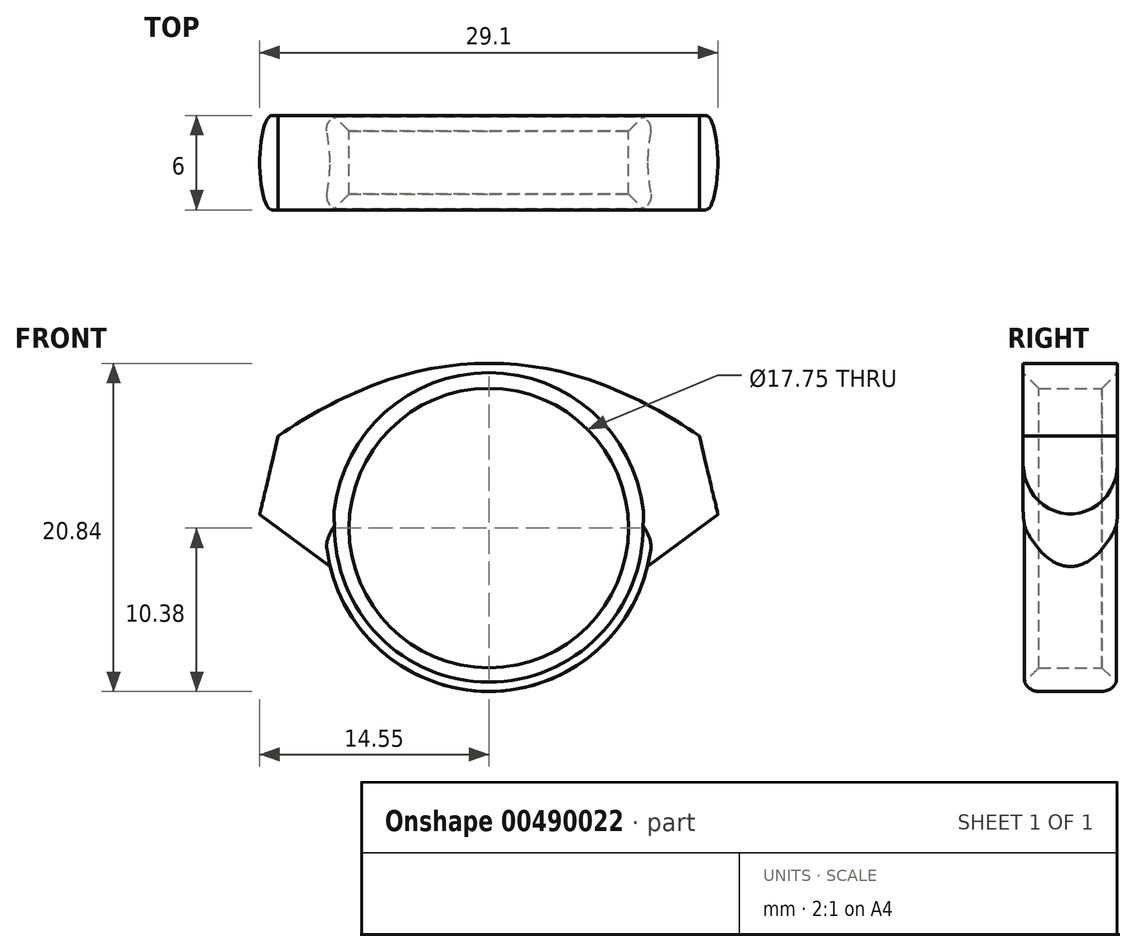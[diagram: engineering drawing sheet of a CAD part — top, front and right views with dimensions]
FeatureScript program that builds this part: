
annotation { "Feature Type Name" : "Feature", "Feature Type Description" : "" }
export const myFeature = defineFeature(function(context is Context, id is Id, definition is map)
    precondition{}
    {
        {
            var Q0;
            Q0=qCreatedBy(makeId("Front.planeOp"),FACE);
            var sketch = newSketch(context, id + "F0", { "sketchPlane" : qUnion([Q0])});
            skCircle(sketch, "E0", {"center": v(0, 0) * mm, "radius": 8.88 * mm});
            skCircle(sketch, "E1.0", {"center": v(0, 0) * mm, "radius": 10.38 * mm});
            skLineSegment(sketch, "E2", {"start": v(-10.08, -2.44) * mm, "end": v(-14.55, 0.87) * mm});
            skLineSegment(sketch, "E3", {"start": v(-14.55, 0.87) * mm, "end": v(-13.37, 5.85) * mm});
            skLineSegment(sketch, "E4", {"start": v(-13.37, 5.85) * mm, "end": v(-10.08, -2.44) * mm});
            skArc(sketch, "E5", {"start": v(0, 10.9) * mm, "mid": v(-7, 9.2) * mm, "end": v(-13.37, 5.85) * mm});
            skArc(sketch, "E6.MirrorCS", {"start": v(0, 10.9) * mm, "mid": v(7, 9.2) * mm, "end": v(13.37, 5.85) * mm});
            skLineSegment(sketch, "E7.MirrorCS", {"start": v(14.55, 0.87) * mm, "end": v(13.37, 5.85) * mm});
            skLineSegment(sketch, "E8.MirrorCS", {"start": v(10.08, -2.44) * mm, "end": v(14.55, 0.87) * mm});
            skSolve(sketch);
        }
        {
            var Q0;
            {var subQ0=sQuery(id+"F0.wireOp",EDGE,"E4");Q0=makeQuery(id+"F0.imprint","IMPRINT",FACE,{"disambiguationData":[TD([[makeQuery(id+"F0.imprint","IMPRINT",EDGE,{"derivedFrom":subQ0}),1.0]])]});}
            var Q1;
            Q1=makeQuery(id+"F0.imprint","IMPRINT",FACE,{"disambiguationData":[TD([[makeQuery(id+"F0.imprint","IMPRINT",EDGE,{"derivedFrom":sQuery(id+"F0.wireOp",EDGE,"E2")}),-1.0]])]});
            var Q2;
            Q2=makeQuery(id+"F0.imprint","IMPRINT",FACE,{"disambiguationData":[TD([[makeQuery(id+"F0.imprint","IMPRINT",EDGE,{"derivedFrom":sQuery(id+"F0.wireOp",EDGE,"E0")}),-1.0]])]});
            extrude(context, id + "F1", {"entities" : qUnion([Q0, Q1, Q2]), "depth" : 3 * mm, "offsetDistance" : 25 * mm, "hasSecondDirection" : true, "secondDirectionOppositeDirection" : true, "secondDirectionDepth" : 3 * mm});
        }
        {
            var Q0;
            Q0=makeQuery(id+"F1.opExtrude","CAP_EDGE",EDGE,{"disambiguationData":[OSD([sQuery(id+"F0.wireOp",EDGE,"E8.MirrorCS")])],"isStart":false});
            var Q1;
            Q1=makeQuery(id+"F1.opExtrude","CAP_EDGE",EDGE,{"disambiguationData":[OSD([sQuery(id+"F0.wireOp",EDGE,"E8.MirrorCS")])],"isStart":true});
            var Q2;
            Q2=makeQuery(id+"F1.opExtrude","CAP_EDGE",EDGE,{"disambiguationData":[OSD([sQuery(id+"F0.wireOp",EDGE,"E2")])],"isStart":false});
            var Q3;
            Q3=makeQuery(id+"F1.opExtrude","CAP_EDGE",EDGE,{"disambiguationData":[OSD([sQuery(id+"F0.wireOp",EDGE,"E2")])],"isStart":true});
            fillet(context, id + "F2", {"entities" : qUnion([Q0, Q1, Q2, Q3]), "radius" : 3 * mm, "tangentPropagation" : true, "allowEdgeOverflow" : false});
        }
        {
            var Q0;
            Q0=makeQuery(id+"F1.opExtrude","CAP_EDGE",EDGE,{"disambiguationData":[OSD([sQuery(id+"F0.wireOp",EDGE,"E0")])],"isStart":false});
            var Q1;
            Q1=makeQuery(id+"F1.opExtrude","CAP_EDGE",EDGE,{"disambiguationData":[OSD([sQuery(id+"F0.wireOp",EDGE,"E0")])],"isStart":true});
            chamfer(context, id + "F3", {"entities" : qUnion([Q0, Q1]), "width" : 1 * mm, "tangentPropagation" : true});
        }
        {
            var Q0;
            Q0=makeQuery(id+"F1.opExtrude","CAP_EDGE",EDGE,{"disambiguationData":[OSD([sQuery(id+"F0.wireOp",EDGE,"E1.0")])],"isStart":true});
            var Q1;
            Q1=makeQuery(id+"F1.opExtrude","CAP_EDGE",EDGE,{"disambiguationData":[OSD([sQuery(id+"F0.wireOp",EDGE,"E1.0")])],"isStart":false});
            fillet(context, id + "F4", {"entities" : qUnion([Q0, Q1]), "radius" : 1 * mm, "tangentPropagation" : true, "allowEdgeOverflow" : false});
        }
        {
            var Q0;
            Q0=makeQuery(id+"F1.opExtrude","SWEPT_EDGE",EDGE,{"disambiguationData":[OSD([sQuery(id+"F0.wireOp",EDGE,"E5"),sQuery(id+"F0.wireOp",EDGE,"E6.MirrorCS")])]});
            fillet(context, id + "F5", {"entities" : qUnion([Q0]), "radius" : 20 * mm, "tangentPropagation" : true, "allowEdgeOverflow" : false});
        }
    });
